# Revit family: Клапан запорный для отключения радиатора HERZ-RL-1, угловой 3724
name_source: partatom
category: Rohrzubehör
units: mm (PartAtom-declared; Revit-internal decimal feet)

## family parameters
Arbeitsebenenbasiert = Nein
Beim Laden mit Abzugskörper schneiden = Nein
Bemaßung runder Anschluss = Durchmesser verwenden
Gemeinsam genutzt = Nein
Immer vertikal = Nein
OmniClass-Nummer = 23.65.55.14
OmniClass-Titel = Valves for Liquid Services
Teiletyp = Unterbricht

## types (1)
- Клапан запорный для отключения радиатора HERZ-RL-1, угловой 3724
    H04 = 25.5 mm
    H05 = 5.2 mm  [stored 0.0170604 ft]
    Hersteller = HERZ Armaturen Ges.m.b.H.
    R01 = 10.5 mm  [stored 0.0344488 ft]
    R06 = 11 mm  [stored 0.0360892 ft]
    S01 = 10 mm  [stored 0.0328084 ft]
    S04 = 45 mm  [stored 0.147638 ft]
    SCRNCODE = 05;01;02
    SCRNSEQ = ARM;ARM_TYP="ALLF";2
    URL = www.herz-armaturen.ru
    Vorgabe-Ansicht = 0 mm  [stored 0 ft]
    Исполнение = Все модели поставляются в никелированном исполнении, это универсальные модели со специальной муфтой для резьбовой трубы и компрессионных фитингов.
    Корпус = Никелированная латунь
    Макс. рабочая температура = 120 °C
    Макс. рабочее давление = 1000000.0 Pa
    Область применения = Система водяного отопления. С помощью установки радиаторных запорных клапанов возможно осуществить перекрытие обратного потока нагревательных приборов. При одновременном перекрытии с клапаном на подающем трубопроводе возможен демонтаж радиатора в системе, которая находится под давлением. Промывку радиатора или ремонт помещения (оклеивание обоями, облицовку плиткой) можно проводить, не прерывая работу системы. Если требуется предварительная настройка клапанов для отключения радиаторов или заполнение и опорожнение радиаторов или системы при помощи данного клапана, рекомендуется установка клапана HERZ-RL-5.
    Среда = Качество воды в соответствии с ÖNORM H 5195 или директивой VDI 2035.

note: [stored X ft] marks values corroborated as IEEE doubles in the binary element streams (Revit-internal decimal feet)
